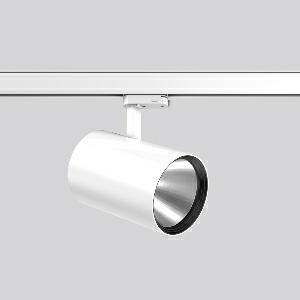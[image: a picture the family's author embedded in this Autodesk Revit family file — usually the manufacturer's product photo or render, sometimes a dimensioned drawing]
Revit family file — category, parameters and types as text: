
# Revit family: deecos_s_maxi_742213_002_1_5174
name_source: partatom
category: Lighting Fixtures
units: mm (PartAtom-declared; Revit-internal decimal feet)

## family parameters
Cut with Voids When Loaded = No
Host = Face
Light Source = No
Part Type = Normal
Room Calculation Point = No
Round Connector Dimension = Use Diameter
Shared = No

## types (1)
- DEECOS S maxi (1 x LED Modul 940, 3400 lm, 4000)
    Apparent Load = 25 VA
    Approval mark = CE
    CIE Flux Codes = 100 100 100 100 100
    Color Rendering = 92
    Color Temperature = 4000
    Default Elevation = 1800 mm
    Description = Series: DEECOS S maxi
LED surface-mounted projector in modern design with no visible cooling ribs. Housing: die-cast aluminium, powder-coated. Rotation range: 356°. Swivel range: 90°. Black plastic ring and recessed LED to prevent glare from the side. Optical assembly with reflector made of MIRO-Silver with 98% total light reflection for outstanding efficiency - can be changed without tools. Best colour rendering index Ra>90. With multi adaptor for 3-circuit tracks 230 V. Suitable for Track on ceiling, Wall track. High quality converter without flickering and stroboscopic effect. The following accessories can be mounted without use of tools: interchangeable lenses, decorative glasses, honeycomb louvre, clear and frosted diffusers, white interchangeable plastic ring. 
Colour: traffic white, matt (RAL 9016)
Diameter: 123 mm
Height: 200 mm
Lamp: LED
Socket: without socket
Colour temperature: 4000K
Colour rendering index (CRI): 92
System power: 25 W
Rated luminous flux: 3400 lm
Luminous efficiency: 136 lm/W
Control gear: Regulated power supply
Protection class: I
Type of protection: IP 20
    Height = 200 mm  [stored 0.656168 ft]
    Lamp = 1 x LED Modul 940
    Lamp Light Flux = 3400 lm
    Lamp count = 1
    Length = 123 mm
    Lifetime = 50000 h
    Luminous efficacy = 136 lm/W
    Manufacturer = RZB
    ModVariant = No
    Model = 742213.002.1
    Mounting Place = Ceiling
    Mounting Type = Rail mounted
    Number of Poles = 1
    OnlyDefault = Yes
    Power Factor = 1
    Product Name = DEECOS S maxi
    Product group = Track mounted projectors
    ProductGroupID = 301
    Protection Class = Protection class I
    Protection Degree = IP 20
    RLX_Detail_Level = 1
    RLX_Emergency_Light_Flux = 0 lm
    RLX_Emergency_Type = 0
    RLX_Emergency_Type_DB = No
    RlxData = <blob elided: 38529 chars, md5=d2b7ce66>
    Socket = socket
    Standby Power = 0 W
    System Light Flux = 3400 lm
    System Power = 25 W
    Type Comments = Product without accessories
    Type Image = 741954.002.jpg
    URL = http://relux.com
    VarID = ---
    Voltage = 230 V
    Voltage Range = 220-240 V
    Weight = 0.00 kg
    Width = 0 mm  [stored 0 ft]

note: [stored X ft] marks values corroborated as IEEE doubles in the binary element streams (Revit-internal decimal feet)

## geometry (parser evidence)
native form markers: Blend x4, Sweep x12
no freeform markers — native parametric forms only
